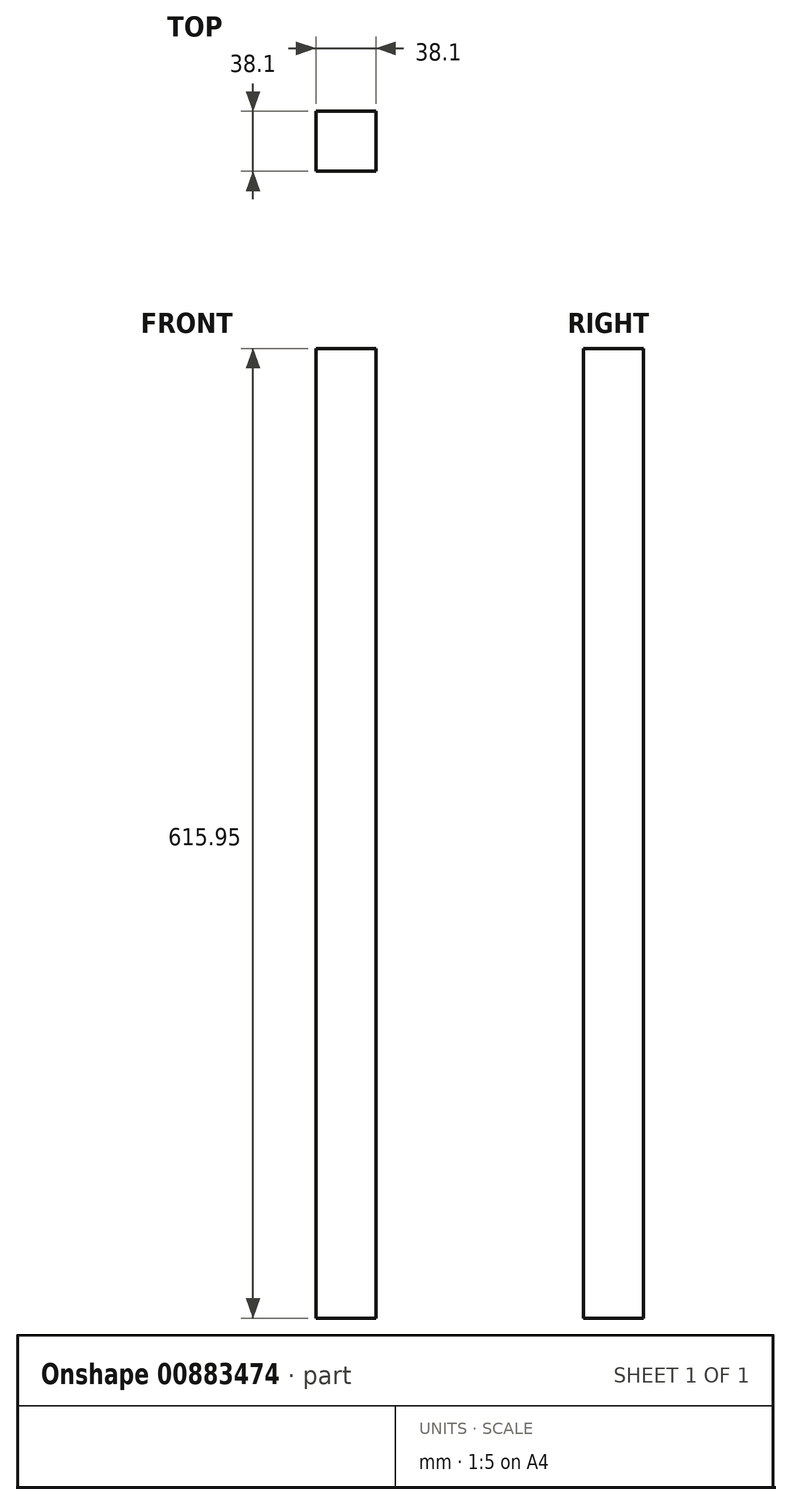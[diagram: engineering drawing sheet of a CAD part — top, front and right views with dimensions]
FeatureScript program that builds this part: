
annotation { "Feature Type Name" : "Feature", "Feature Type Description" : "" }
export const myFeature = defineFeature(function(context is Context, id is Id, definition is map)
    precondition{}
    {
        {
            var Q0;
            Q0=qCreatedBy(makeId("Top.planeOp"),FACE);
            var sketch = newSketch(context, id + "F0", { "sketchPlane" : qUnion([Q0])});
            skLineSegment(sketch, "E0.bottom", {"start": v(0, 0) * mm, "end": v(38.1, 0) * mm});
            skLineSegment(sketch, "E0.top", {"start": v(0, 38.1) * mm, "end": v(38.1, 38.1) * mm});
            skLineSegment(sketch, "E0.left", {"start": v(0, 0) * mm, "end": v(0, 38.1) * mm});
            skLineSegment(sketch, "E0.right", {"start": v(38.1, 0) * mm, "end": v(38.1, 38.1) * mm});
            skSolve(sketch);
        }
        {
            var Q0;
            Q0 = qSketchRegion(id + "F0", true);
            extrude(context, id + "F1", {"entities" : qUnion([Q0]), "depth" : 615.95 * mm, "offsetDistance" : 25.4 * mm});
        }
    });
